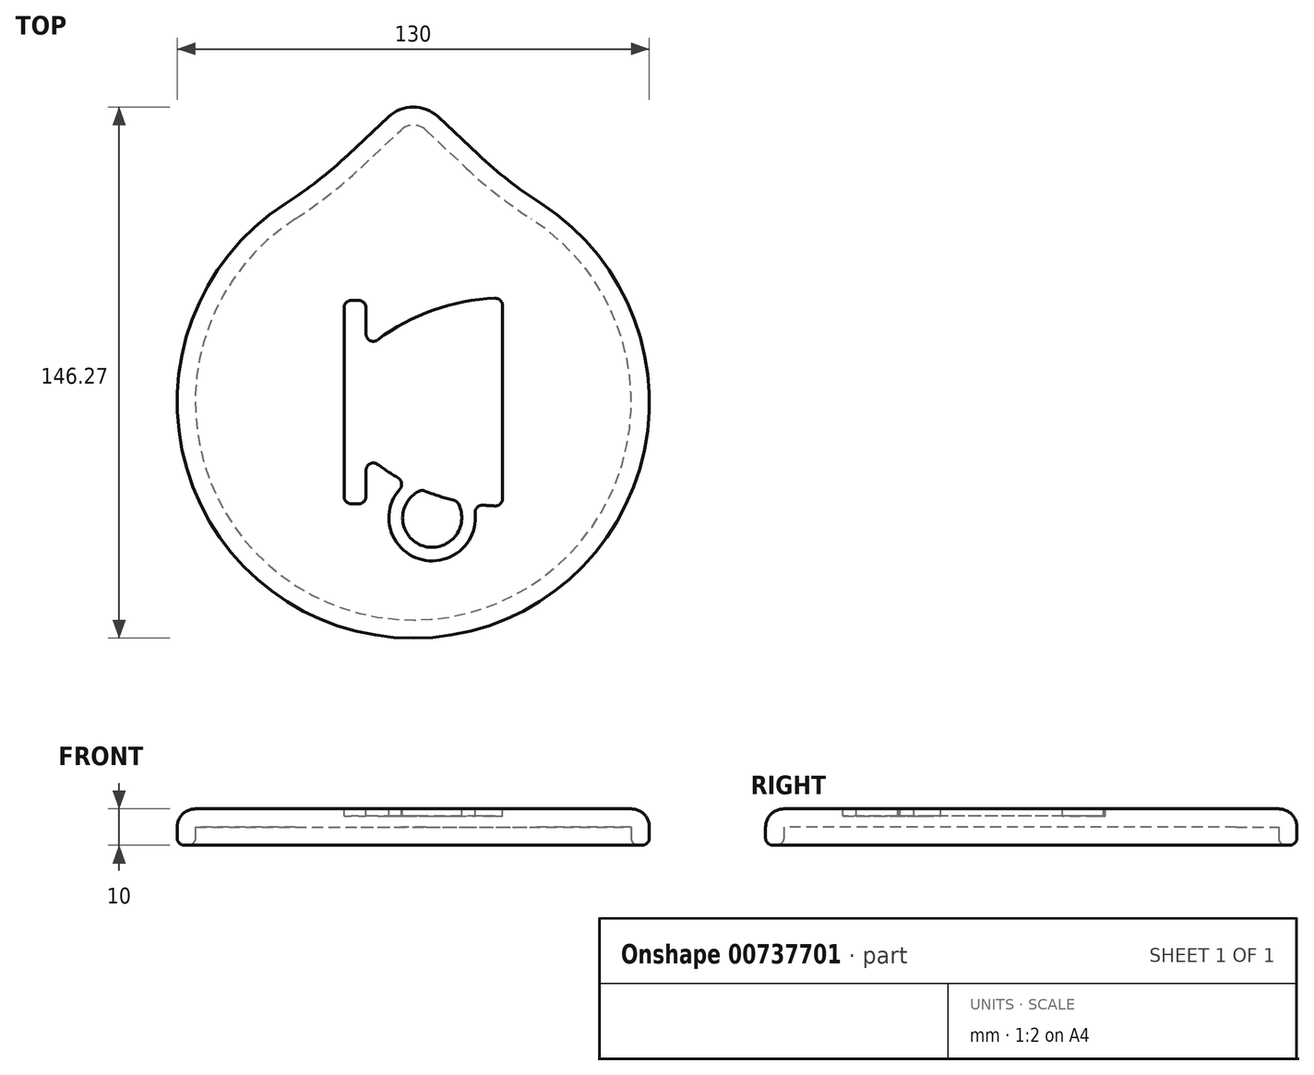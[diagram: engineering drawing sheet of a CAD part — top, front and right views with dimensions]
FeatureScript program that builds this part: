
annotation { "Feature Type Name" : "Feature", "Feature Type Description" : "" }
export const myFeature = defineFeature(function(context is Context, id is Id, definition is map)
    precondition{}
    {
        {
            var Q0;
            Q0=qCreatedBy(makeId("Top.planeOp"),FACE);
            var sketch = newSketch(context, id + "F0", { "sketchPlane" : qUnion([Q0])});
            skCircle(sketch, "E0", {"center": v(0, 0) * mm, "radius": 65 * mm, "construction": true});
            skLineSegment(sketch, "E1", {"start": v(-28, 58.66) * mm, "end": v(0, 85) * mm});
            skLineSegment(sketch, "E2", {"start": v(0, 85) * mm, "end": v(28, 58.66) * mm});
            skArc(sketch, "E3", {"start": v(-28, 58.66) * mm, "mid": v(0, -65) * mm, "end": v(28, 58.66) * mm});
            skSolve(sketch);
        }
        {
            var Q0;
            Q0 = qSketchRegion(id + "F0", true);
            extrude(context, id + "F1", {"entities" : qUnion([Q0]), "depth" : 10 * mm, "offsetDistance" : 25 * mm});
        }
        {
            var Q0;
            Q0=makeQuery(id+"F1.opExtrude","SWEPT_EDGE",EDGE,{"disambiguationData":[OSD([sQuery(id+"F0.wireOp",EDGE,"E1"),sQuery(id+"F0.wireOp",EDGE,"E2")])]});
            fillet(context, id + "F2", {"entities" : qUnion([Q0]), "radius" : 10 * mm, "tangentPropagation" : true, "allowEdgeOverflow" : false});
        }
        {
            var Q0;
            Q0=makeQuery(id+"F1.opExtrude","SWEPT_EDGE",EDGE,{"disambiguationData":[OSD([sQuery(id+"F0.wireOp",EDGE,"E1"),sQuery(id+"F0.wireOp",EDGE,"E3")])]});
            var Q1;
            Q1=makeQuery(id+"F1.opExtrude","SWEPT_EDGE",EDGE,{"disambiguationData":[OSD([sQuery(id+"F0.wireOp",EDGE,"E2"),sQuery(id+"F0.wireOp",EDGE,"E3")])]});
            fillet(context, id + "F3", {"entities" : qUnion([Q0, Q1]), "radius" : 120 * mm, "tangentPropagation" : true, "allowEdgeOverflow" : false});
        }
        {
            var Q0;
            Q0=makeQuery(id+"F1.opExtrude","CAP_FACE",FACE,{"disambiguationData":[OSD([sQuery(id+"F0.wireOp",EDGE,"E1"),sQuery(id+"F0.wireOp",EDGE,"E2"),sQuery(id+"F0.wireOp",EDGE,"E3")])],"isStart":true});
            shell(context, id + "F4", {"entities" : qUnion([Q0]), "thickness" : 5 * mm});
        }
        {
            var Q0;
            Q0=makeQuery(id+"F1.opExtrude","CAP_EDGE",EDGE,{"disambiguationData":[OSD([sQuery(id+"F0.wireOp",EDGE,"E3")])],"isStart":false});
            fillet(context, id + "F5", {"entities" : qUnion([Q0]), "radius" : 5 * mm, "tangentPropagation" : true, "allowEdgeOverflow" : false});
        }
        {
            var Q0;
            Q0=makeQuery(id+"F1.opExtrude","CAP_FACE",FACE,{"disambiguationData":[OSD([sQuery(id+"F0.wireOp",EDGE,"E1"),sQuery(id+"F0.wireOp",EDGE,"E2"),sQuery(id+"F0.wireOp",EDGE,"E3")])],"isStart":false});
            var sketch = newSketch(context, id + "F6", { "sketchPlane" : qUnion([Q0])});
            skLineSegment(sketch, "E4", {"start": v(24.58, 28.62) * mm, "end": v(24.58, -28.62) * mm});
            skArc(sketch, "E5", {"start": v(24.58, 28.62) * mm, "mid": v(4.51, 25) * mm, "end": v(-13, 14.55) * mm});
            skArc(sketch, "E6", {"start": v(-13, -14.55) * mm, "mid": v(-7.62, -18.7) * mm, "end": v(-1.78, -22.2) * mm});
            skLineSegment(sketch, "E7", {"start": v(-13, 14.55) * mm, "end": v(-13, 28) * mm});
            skLineSegment(sketch, "E8", {"start": v(-13, 28) * mm, "end": v(-19.06, 28) * mm});
            skLineSegment(sketch, "E9", {"start": v(-19.06, 28) * mm, "end": v(-19.06, -28) * mm});
            skLineSegment(sketch, "E10", {"start": v(-19.06, -28) * mm, "end": v(-13, -28) * mm});
            skLineSegment(sketch, "E11", {"start": v(-13, -28) * mm, "end": v(-13, -14.55) * mm});
            skArc(sketch, "E12", {"start": v(-1.78, -22.2) * mm, "mid": v(1.58, -43.16) * mm, "end": v(16.5, -28.05) * mm});
            skArc(sketch, "E13", {"start": v(2.42, -24.16) * mm, "mid": v(2.72, -39.6) * mm, "end": v(11.93, -27.2) * mm});
            skArc(sketch, "E14.trimOffspring", {"start": v(16.5, -28.05) * mm, "mid": v(20.53, -28.48) * mm, "end": v(24.58, -28.62) * mm});
            skArc(sketch, "E15.trimOffspring", {"start": v(2.42, -24.16) * mm, "mid": v(7.11, -25.9) * mm, "end": v(11.93, -27.2) * mm});
            skSolve(sketch);
        }
        {
            var Q0;
            Q0 = qSketchRegion(id + "F6", true);
            extrude(context, id + "F7", {"entities" : qUnion([Q0]), "operationType" : NewBodyOperationType.REMOVE, "oppositeDirection" : true, "depth" : 2 * mm, "offsetDistance" : 25 * mm});
        }
        {
            var Q0;
            Q0=makeQuery(id+"F7.boolean.opBoolean","COPY",EDGE,{"derivedFrom":makeQuery(id+"F7.opExtrude","SWEPT_EDGE",EDGE,{"disambiguationData":[OSD([sQuery(id+"F6.wireOp",EDGE,"E7"),sQuery(id+"F6.wireOp",EDGE,"E8")])]})});
            var Q1;
            Q1=makeQuery(id+"F7.boolean.opBoolean","COPY",EDGE,{"derivedFrom":makeQuery(id+"F7.opExtrude","SWEPT_EDGE",EDGE,{"disambiguationData":[OSD([sQuery(id+"F6.wireOp",EDGE,"E8"),sQuery(id+"F6.wireOp",EDGE,"E9")])]})});
            var Q2;
            Q2=makeQuery(id+"F7.boolean.opBoolean","COPY",EDGE,{"derivedFrom":makeQuery(id+"F7.opExtrude","SWEPT_EDGE",EDGE,{"disambiguationData":[OSD([sQuery(id+"F6.wireOp",EDGE,"E5"),sQuery(id+"F6.wireOp",EDGE,"E7")])]})});
            var Q3;
            Q3=makeQuery(id+"F7.boolean.opBoolean","COPY",EDGE,{"derivedFrom":makeQuery(id+"F7.opExtrude","SWEPT_EDGE",EDGE,{"disambiguationData":[OSD([sQuery(id+"F6.wireOp",EDGE,"E4"),sQuery(id+"F6.wireOp",EDGE,"E5")])]})});
            var Q4;
            Q4=makeQuery(id+"F7.boolean.opBoolean","COPY",EDGE,{"derivedFrom":makeQuery(id+"F7.opExtrude","SWEPT_EDGE",EDGE,{"disambiguationData":[OSD([sQuery(id+"F6.wireOp",EDGE,"E4"),sQuery(id+"F6.wireOp",EDGE,"E14.trimOffspring")])]})});
            var Q5;
            Q5=makeQuery(id+"F7.boolean.opBoolean","COPY",EDGE,{"derivedFrom":makeQuery(id+"F7.opExtrude","SWEPT_EDGE",EDGE,{"disambiguationData":[OSD([sQuery(id+"F6.wireOp",EDGE,"E12"),sQuery(id+"F6.wireOp",EDGE,"E14.trimOffspring")])]})});
            var Q6;
            Q6=makeQuery(id+"F7.boolean.opBoolean","COPY",EDGE,{"derivedFrom":makeQuery(id+"F7.opExtrude","SWEPT_EDGE",EDGE,{"disambiguationData":[OSD([sQuery(id+"F6.wireOp",EDGE,"E6"),sQuery(id+"F6.wireOp",EDGE,"E12")])]})});
            var Q7;
            {var subQ0=sQuery(id+"F6.wireOp",EDGE,"E15.trimOffspring");var subQ1=sQuery(id+"F6.wireOp",EDGE,"E13");Q7=makeQuery(id+"F7.boolean.opBoolean","COPY",EDGE,{"derivedFrom":makeQuery(id+"F7.opExtrude","SWEPT_EDGE",EDGE,{"disambiguationData":[OSD([subQ1,subQ0]),TDD([makeQuery(id+"F6.imprint","INTERSECT",VERTEX,{"disambiguationData":[OD(0.0)],"derivedFrom":[subQ1,subQ0]})])]})});}
            var Q8;
            {var subQ0=sQuery(id+"F6.wireOp",EDGE,"E15.trimOffspring");var subQ1=sQuery(id+"F6.wireOp",EDGE,"E13");Q8=makeQuery(id+"F7.boolean.opBoolean","COPY",EDGE,{"derivedFrom":makeQuery(id+"F7.opExtrude","SWEPT_EDGE",EDGE,{"disambiguationData":[OSD([subQ1,subQ0]),TDD([makeQuery(id+"F6.imprint","INTERSECT",VERTEX,{"disambiguationData":[OD(1.0)],"derivedFrom":[subQ1,subQ0]})])]})});}
            var Q9;
            Q9=makeQuery(id+"F7.boolean.opBoolean","COPY",EDGE,{"derivedFrom":makeQuery(id+"F7.opExtrude","SWEPT_EDGE",EDGE,{"disambiguationData":[OSD([sQuery(id+"F6.wireOp",EDGE,"E6"),sQuery(id+"F6.wireOp",EDGE,"E11")])]})});
            var Q10;
            Q10=makeQuery(id+"F7.boolean.opBoolean","COPY",EDGE,{"derivedFrom":makeQuery(id+"F7.opExtrude","SWEPT_EDGE",EDGE,{"disambiguationData":[OSD([sQuery(id+"F6.wireOp",EDGE,"E10"),sQuery(id+"F6.wireOp",EDGE,"E11")])]})});
            var Q11;
            Q11=makeQuery(id+"F7.boolean.opBoolean","COPY",EDGE,{"derivedFrom":makeQuery(id+"F7.opExtrude","SWEPT_EDGE",EDGE,{"disambiguationData":[OSD([sQuery(id+"F6.wireOp",EDGE,"E9"),sQuery(id+"F6.wireOp",EDGE,"E10")])]})});
            fillet(context, id + "F8", {"entities" : qUnion([Q0, Q1, Q2, Q3, Q4, Q5, Q6, Q7, Q8, Q9, Q10, Q11]), "radius" : 2 * mm, "tangentPropagation" : true, "allowEdgeOverflow" : false});
        }
        {
            var Q0;
            {var subQ0=sQuery(id+"F0.wireOp",EDGE,"E3");Q0=makeQuery(id+"F4.opShell","OFFSET_EDGE",EDGE,{"disambiguationData":[OSD([subQ0]),TDD([makeQuery(id+"F1.opExtrude","CAP_EDGE",EDGE,{"disambiguationData":[OSD([subQ0])],"isStart":true})])]});}
            var Q1;
            Q1=makeQuery(id+"F1.opExtrude","CAP_EDGE",EDGE,{"disambiguationData":[OSD([sQuery(id+"F0.wireOp",EDGE,"E3")])],"isStart":true});
            fillet(context, id + "F9", {"entities" : qUnion([Q0, Q1]), "radius" : 2 * mm, "tangentPropagation" : true, "allowEdgeOverflow" : false});
        }
    });
